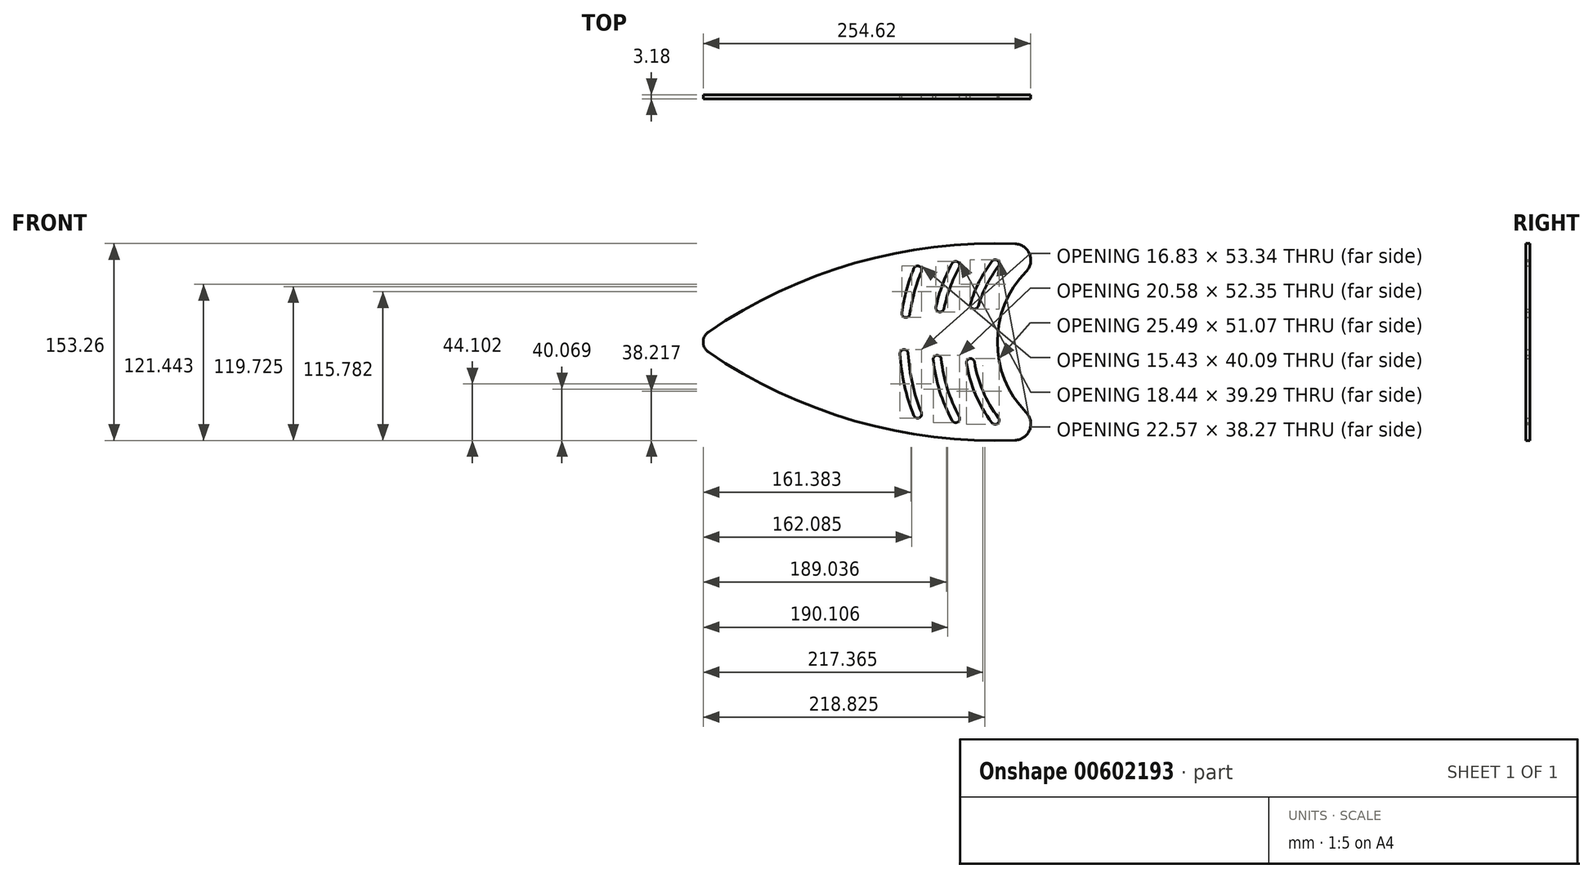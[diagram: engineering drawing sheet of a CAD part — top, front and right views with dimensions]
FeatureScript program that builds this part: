
annotation { "Feature Type Name" : "Feature", "Feature Type Description" : "" }
export const myFeature = defineFeature(function(context is Context, id is Id, definition is map)
    precondition{}
    {
        {
            var Q0;
            Q0=qCreatedBy(makeId("Front.planeOp"),FACE);
            var sketch = newSketch(context, id + "F0", { "sketchPlane" : qUnion([Q0])});
            skArc(sketch, "E0", {"start": v(96.92, 56.72) * mm, "mid": v(87.03, 40.98) * mm, "end": v(80.12, 23.72) * mm});
            skArc(sketch, "E1", {"start": v(65.86, 55.08) * mm, "mid": v(58.42, 38.6) * mm, "end": v(53.36, 21.22) * mm});
            skArc(sketch, "E2", {"start": v(36.16, 51.2) * mm, "mid": v(30.5, 34.22) * mm, "end": v(26.83, 16.69) * mm});
            skArc(sketch, "E3", {"start": v(42.03, 48.85) * mm, "mid": v(36.6, 32.57) * mm, "end": v(33.09, 15.76) * mm});
            skArc(sketch, "E4", {"start": v(71.43, 52.08) * mm, "mid": v(64.35, 36.4) * mm, "end": v(59.55, 19.88) * mm});
            skArc(sketch, "E5", {"start": v(31.74, -14.84) * mm, "mid": v(28.4, -11.87) * mm, "end": v(25.43, -15.22) * mm});
            skArc(sketch, "E6", {"start": v(31.74, -14.84) * mm, "mid": v(35.04, -38.27) * mm, "end": v(42.03, -60.87) * mm});
            skArc(sketch, "E7", {"start": v(25.43, -15.22) * mm, "mid": v(28.87, -39.65) * mm, "end": v(36.16, -63.22) * mm});
            skArc(sketch, "E8", {"start": v(57.5, -19.2) * mm, "mid": v(54, -16.4) * mm, "end": v(51.2, -19.88) * mm});
            skArc(sketch, "E9", {"start": v(83.33, -21.5) * mm, "mid": v(79.7, -18.89) * mm, "end": v(77.08, -22.52) * mm});
            skArc(sketch, "E10", {"start": v(26.83, 16.69) * mm, "mid": v(29.5, 13.1) * mm, "end": v(33.09, 15.76) * mm});
            skArc(sketch, "E11", {"start": v(53.36, 21.22) * mm, "mid": v(55.79, 17.46) * mm, "end": v(59.55, 19.88) * mm});
            skArc(sketch, "E12", {"start": v(80.12, 23.72) * mm, "mid": v(82.24, 19.78) * mm, "end": v(86.18, 21.9) * mm});
            skArc(sketch, "E13", {"start": v(51.2, -19.88) * mm, "mid": v(56.24, -44.2) * mm, "end": v(65.86, -67.1) * mm});
            skArc(sketch, "E14", {"start": v(57.5, -19.2) * mm, "mid": v(62.29, -42.32) * mm, "end": v(71.43, -64.1) * mm});
            skArc(sketch, "E15", {"start": v(83.33, -21.5) * mm, "mid": v(89.96, -44.35) * mm, "end": v(101.95, -64.9) * mm});
            skArc(sketch, "E16", {"start": v(77.08, -22.52) * mm, "mid": v(84.15, -46.85) * mm, "end": v(96.92, -68.74) * mm});
            skArc(sketch, "E17", {"start": v(36.16, -63.22) * mm, "mid": v(40.27, -64.98) * mm, "end": v(42.03, -60.87) * mm});
            skArc(sketch, "E18", {"start": v(65.86, -67.1) * mm, "mid": v(70.14, -68.38) * mm, "end": v(71.43, -64.1) * mm});
            skArc(sketch, "E19", {"start": v(96.92, -68.74) * mm, "mid": v(101.35, -69.34) * mm, "end": v(101.95, -64.9) * mm});
            skArc(sketch, "E20", {"start": v(42.03, 48.85) * mm, "mid": v(40.27, 52.96) * mm, "end": v(36.16, 51.2) * mm});
            skArc(sketch, "E21", {"start": v(71.43, 52.08) * mm, "mid": v(70.14, 56.37) * mm, "end": v(65.86, 55.08) * mm});
            skArc(sketch, "E22", {"start": v(101.95, 52.89) * mm, "mid": v(101.35, 57.32) * mm, "end": v(96.92, 56.72) * mm});
            skArc(sketch, "E23", {"start": v(101.95, 52.89) * mm, "mid": v(92.67, 38.1) * mm, "end": v(86.18, 21.9) * mm});
            skArc(sketch, "E24", {"start": v(-123.4, -13.84) * mm, "mid": v(-9.76, -67.32) * mm, "end": v(114.94, -82.32) * mm});
            skArc(sketch, "E25", {"start": v(114.94, -82.32) * mm, "mid": v(126.19, -74.34) * mm, "end": v(123.46, -60.82) * mm});
            skArc(sketch, "E26", {"start": v(123.46, -60.82) * mm, "mid": v(101.06, -6) * mm, "end": v(123.46, 48.8) * mm});
            skArc(sketch, "E27", {"start": v(123.46, 48.8) * mm, "mid": v(126.19, 62.32) * mm, "end": v(114.94, 70.3) * mm});
            skArc(sketch, "E28", {"start": v(114.94, 70.3) * mm, "mid": v(-9.76, 55.3) * mm, "end": v(-123.4, 1.82) * mm});
            skArc(sketch, "E29", {"start": v(-123.4, 1.82) * mm, "mid": v(-127.54, -6) * mm, "end": v(-123.4, -13.84) * mm});
            skSolve(sketch);
        }
        {
            var Q0;
            Q0=makeQuery(id+"F0.imprint","IMPRINT",FACE,{"disambiguationData":[TD([[makeQuery(id+"F0.imprint","IMPRINT",EDGE,{"derivedFrom":sQuery(id+"F0.wireOp",EDGE,"E0")}),-1.0]])]});
            extrude(context, id + "F1", {"entities" : qUnion([Q0]), "depth" : 3.17 * mm, "offsetDistance" : 25.4 * mm});
        }
    });
